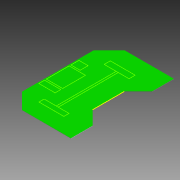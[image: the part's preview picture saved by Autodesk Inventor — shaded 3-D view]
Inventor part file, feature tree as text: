
AUTODESK INVENTOR PART (.ipt)
format: ipt  version: 2015 (Build 190159000, 159)  size: 688,128 bytes
history: native  units: mm
features: sketch x2, plane x1, extrude x1
ambient origin geometry x8: Origin, YZ Plane, XZ Plane, XY Plane, X Axis, Y Axis, Z Axis, Center Point
bodies: Solid1_1 (feature_tree)
feature tree (4):
  plane  "Work Plane3"
  extrude  "Extrusion1"  Depth=5.0mm
  sketch  "Sketch3"  dims[d3=1080.0mm d4=135.0deg d5=328.284271mm d6=328.284271mm d7=740.0mm d8=135.0deg d9=135.0deg d10=135.0deg d11=765.857864mm d12=977.989899mm d13=1555.979797mm]
  sketch  "Sketch1"  dims[d0=5.0mm d1=0.0mm d2=740.0mm]
